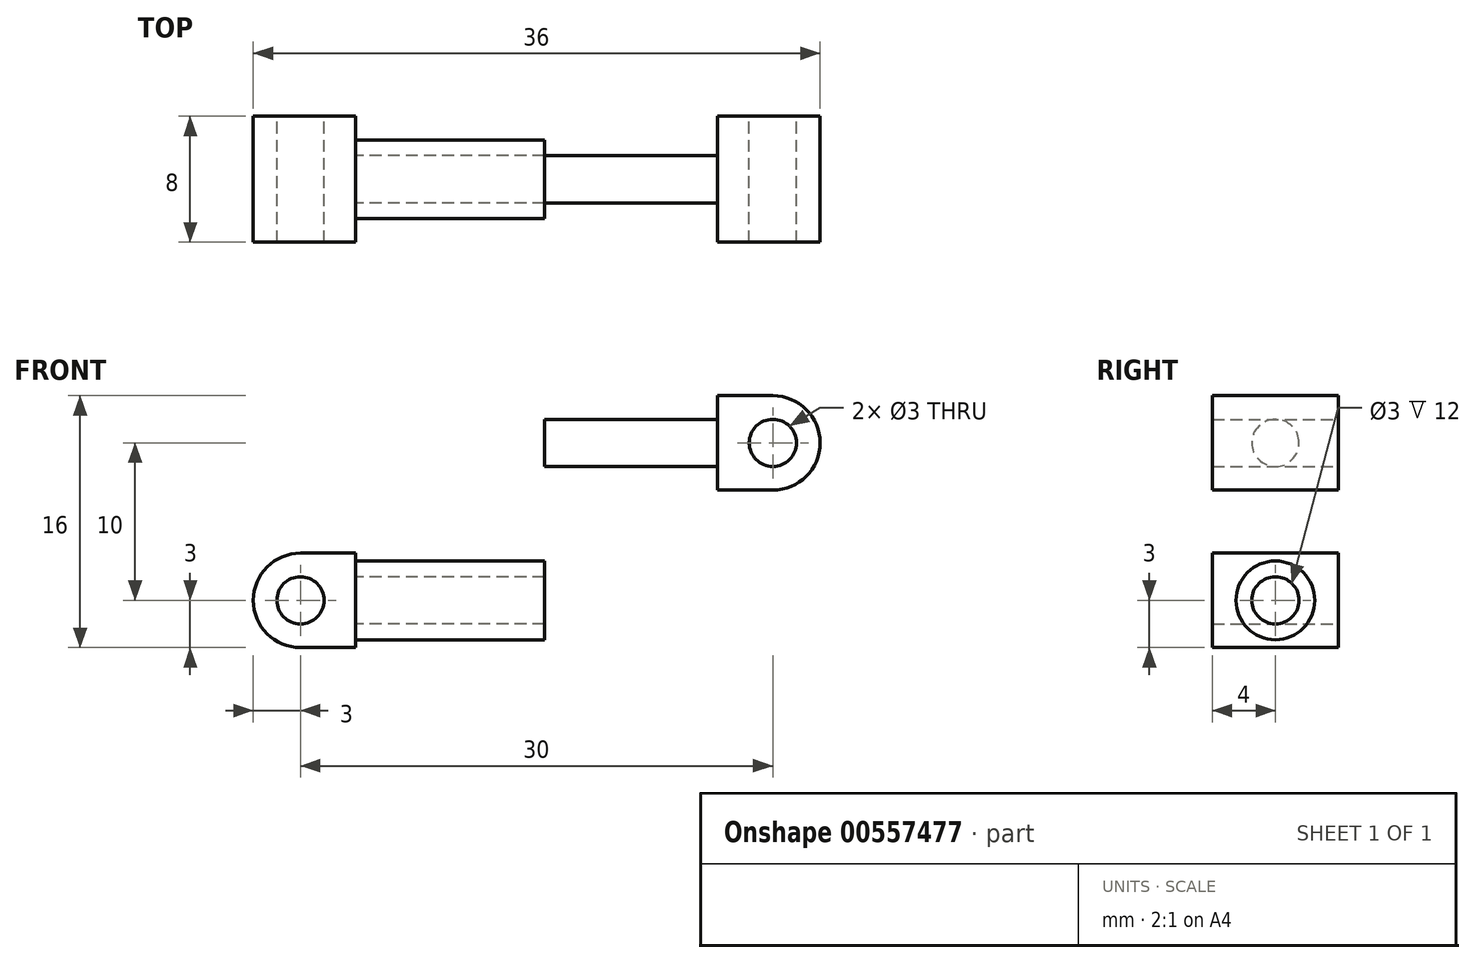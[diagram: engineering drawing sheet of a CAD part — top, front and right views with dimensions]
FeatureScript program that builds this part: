
annotation { "Feature Type Name" : "Feature", "Feature Type Description" : "" }
export const myFeature = defineFeature(function(context is Context, id is Id, definition is map)
    precondition{}
    {
        {
            var Q0;
            Q0=qCreatedBy(makeId("Front.planeOp"),FACE);
            var sketch = newSketch(context, id + "F0", { "sketchPlane" : qUnion([Q0])});
            skCircle(sketch, "E0", {"center": v(0, 0) * mm, "radius": 1.5 * mm});
            skArc(sketch, "E1", {"start": v(0, 3) * mm, "mid": v(-3, 0) * mm, "end": v(0, -3) * mm});
            skLineSegment(sketch, "E2", {"start": v(0, 3) * mm, "end": v(3.5, 3) * mm});
            skLineSegment(sketch, "E3", {"start": v(3.5, 3) * mm, "end": v(3.5, -3) * mm});
            skLineSegment(sketch, "E4", {"start": v(3.5, -3) * mm, "end": v(0, -3) * mm});
            skLineSegment(sketch, "E5", {"start": v(-4.5, 0) * mm, "end": v(45.8, 0) * mm, "construction": true});
            skCircle(sketch, "E6", {"center": v(30, 10) * mm, "radius": 1.5 * mm});
            skArc(sketch, "E7", {"start": v(30, 7) * mm, "mid": v(33, 10) * mm, "end": v(30, 13) * mm});
            skLineSegment(sketch, "E8", {"start": v(30, 7) * mm, "end": v(26.5, 7) * mm});
            skLineSegment(sketch, "E9", {"start": v(26.5, 7) * mm, "end": v(26.5, 13) * mm});
            skLineSegment(sketch, "E10", {"start": v(26.5, 13) * mm, "end": v(30, 13) * mm});
            skLineSegment(sketch, "E11", {"start": v(26.5, 10) * mm, "end": v(15.5, 10) * mm});
            skPoint(sketch, "E11.endSnap0", {"position": v(26.5, 10) * mm});
            skLineSegment(sketch, "E12", {"start": v(15.5, 10) * mm, "end": v(15.5, 11.5) * mm});
            skLineSegment(sketch, "E13", {"start": v(15.5, 11.5) * mm, "end": v(26.5, 11.5) * mm});
            skLineSegment(sketch, "E14", {"start": v(3.5, 1.5) * mm, "end": v(15.5, 1.5) * mm});
            skLineSegment(sketch, "E15", {"start": v(15.5, 1.5) * mm, "end": v(15.5, 2.5) * mm});
            skLineSegment(sketch, "E16", {"start": v(15.5, 2.5) * mm, "end": v(3.5, 2.5) * mm});
            skSolve(sketch);
        }
        {
            var Q0;
            Q0=makeQuery(id+"F0.imprint","IMPRINT",FACE,{"disambiguationData":[TD([[makeQuery(id+"F0.imprint","IMPRINT",EDGE,{"derivedFrom":sQuery(id+"F0.wireOp",EDGE,"E6")}),-1.0]])]});
            var Q1;
            Q1=makeQuery(id+"F0.imprint","IMPRINT",FACE,{"disambiguationData":[TD([[makeQuery(id+"F0.imprint","IMPRINT",EDGE,{"derivedFrom":sQuery(id+"F0.wireOp",EDGE,"E0")}),-1.0]])]});
            extrude(context, id + "F1", {"entities" : qUnion([Q0, Q1]), "endBound" : BoundingType.SYMMETRIC, "depth" : 8 * mm, "offsetDistance" : 25 * mm});
        }
        {
            var Q0;
            {var subQ0=sQuery(id+"F0.wireOp",EDGE,"E14");Q0=makeQuery(id+"F0.imprint","IMPRINT",FACE,{"disambiguationData":[TD([[makeQuery(id+"F0.imprint","IMPRINT",EDGE,{"derivedFrom":subQ0}),1.0]])]});}
            var Q1;
            Q1=sQuery(id+"F0.wireOp",EDGE,"E5");
            revolve(context, id + "F2", {"operationType" : NewBodyOperationType.ADD, "entities" : qUnion([Q0]), "axis" : qUnion([Q1]), "revolveType" : RevolveType.FULL});
        }
        {
            var Q0;
            {var subQ0=sQuery(id+"F0.wireOp",EDGE,"E11");Q0=makeQuery(id+"F0.imprint","IMPRINT",FACE,{"disambiguationData":[TD([[makeQuery(id+"F0.imprint","IMPRINT",EDGE,{"derivedFrom":subQ0}),-1.0]])]});}
            var Q1;
            Q1=sQuery(id+"F0.wireOp",EDGE,"E11");
            revolve(context, id + "F3", {"operationType" : NewBodyOperationType.ADD, "entities" : qUnion([Q0]), "axis" : qUnion([Q1]), "revolveType" : RevolveType.FULL});
        }
    });
